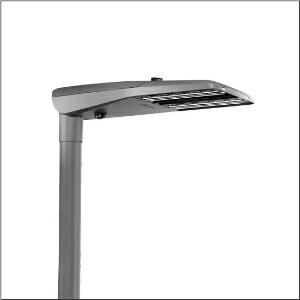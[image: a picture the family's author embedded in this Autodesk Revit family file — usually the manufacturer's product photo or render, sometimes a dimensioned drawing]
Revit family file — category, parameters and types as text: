
# Revit family: streetlight_sl_11_iq_midi___st1_0a_5xc3m51y08le_e71b
name_source: partatom
category: Lighting Fixtures
units: mm (PartAtom-declared; Revit-internal decimal feet)

## family parameters
Cut with Voids When Loaded = No
Host = Face
Light Source = No
Part Type = Normal
Room Calculation Point = No
Round Connector Dimension = Use Diameter
Shared = No

## types (1)
- --- (1 x LED, 8920 lm, 59.4 W, 3000K)
    Apparent Load = 59 VA
    CIE Flux Codes = 33 66 96 100 100
    Color Rendering = 70
    Color Temperature = 3000K
    Default Elevation = 1800 mm
    Description = Streetlight SL 11 iQ midi, mast luminaire, primary light control with 3 zone facetted reflector, of plastic, silver coated, highly specular, primary optical cover: cover, of PMMA, transparent, light distribution: ST1.0a, light emission: direct distribution, primary light characteristic: asymmetric, installation type: post-top, side-entry, LED, High Power LED, rated luminous flux: 8.920lm, luminous efficacy: 150lm/W, light colour: 730, colour temperature: 3000K, control: presetting dimming logarithmic, Street-Remote, Auto-Match, Temp-Guard, Lumen-Switch, Night-Set, Smart-Wire, Light-Fading, Desk-Remote (wireless, voltage-free reading and setting of iQ features in the workshop via application-optimized NFC function/RFID function), optimised constant luminous flux control (CLO 2.0), with cable H07RN-F 5x 1.5mm², mains connection: 230..240V, AC, 50/60Hz, connection cable pre-assembled, cable length: 8,5m, start of lifetime: 59W, end of service life: 62W, reduction: 29W, luminaire housing, of diecast aluminium, powder-coated, Siteco® metallic grey (DB 702S), please order mast flange separately, inclination adjustable without tools: 0°, 5°, 10°, 15° (post-top) | 0°, -5°, -10°, -15° (side-entry), sealing non-destructively replaceable, multi-level sealing system, length: 780mm, width: 376mm, height: 118mm, mast flange for spigot size: 42mm (side-entry): 5XC10008XM4, 60/48mm (side-entry/post-top): 5XC10108XM2, 76/60mm (side-entry/post-top): 5XC10108XM1, equipment: standard, Smart Interface below and above, protection rating (complete): IP66, insulation class (complete): insulation class II (safety insulation), certification: CE, ENEC, VDE, UKCA, impact resistance: IK09, permissible operating ambient temperature for outdoor applications: -25..+50°C, standard-compliant lighting for roads and squares, Environmental Product Declaration (EPD) tested and certified by an independent institute, packaging unit: 1 piece

Light Distribution: ST1.0a
    Height = 118 mm
    Lamp = 1 x LED
    Lamp Light Flux = 8920 lm
    Lamp Power = 59.4 W
    Lamp count = 1
    Length = 780 mm
    Luminous efficacy = 150 lm/W
    Manufacturer = Siteco
    ModVariant = No
    Model = 5XC3M51Y08LE
    Number of Poles = 1
    OnlyDefault = Yes
    Power Factor = 1
    Product Name = Streetlight SL 11 iQ midi | ST1.0a
    Product group = mast luminaire | pylon top
    ProductGroupID = 6100
    Protection Class = Protection class II
    Protection Degree = IP 66
    RLX_Detail_Level = 1
    RLX_Emergency_Light_Flux = 0 lm
    RLX_Emergency_Type = 0
    RLX_Emergency_Type_DB = No
    RlxData = <blob elided: 69093 chars, md5=88933588>
    Socket = socket
    Standby Power = 0 W
    System Light Flux = 8920 lm
    System Power = 59 W
    Type Comments = factory setting: luminous flux: 100 % | dim-lin: 254 | 521 mA
    Type Image = l_1004429.jpg
    URL = http://relux.com
    VarID = @adj_020739
    Voltage = 0 V
    Weight = 0.00 kg
    Width = 376 mm

## geometry (parser evidence)
native form markers: Blend x4, Sweep x10
no freeform markers — native parametric forms only
